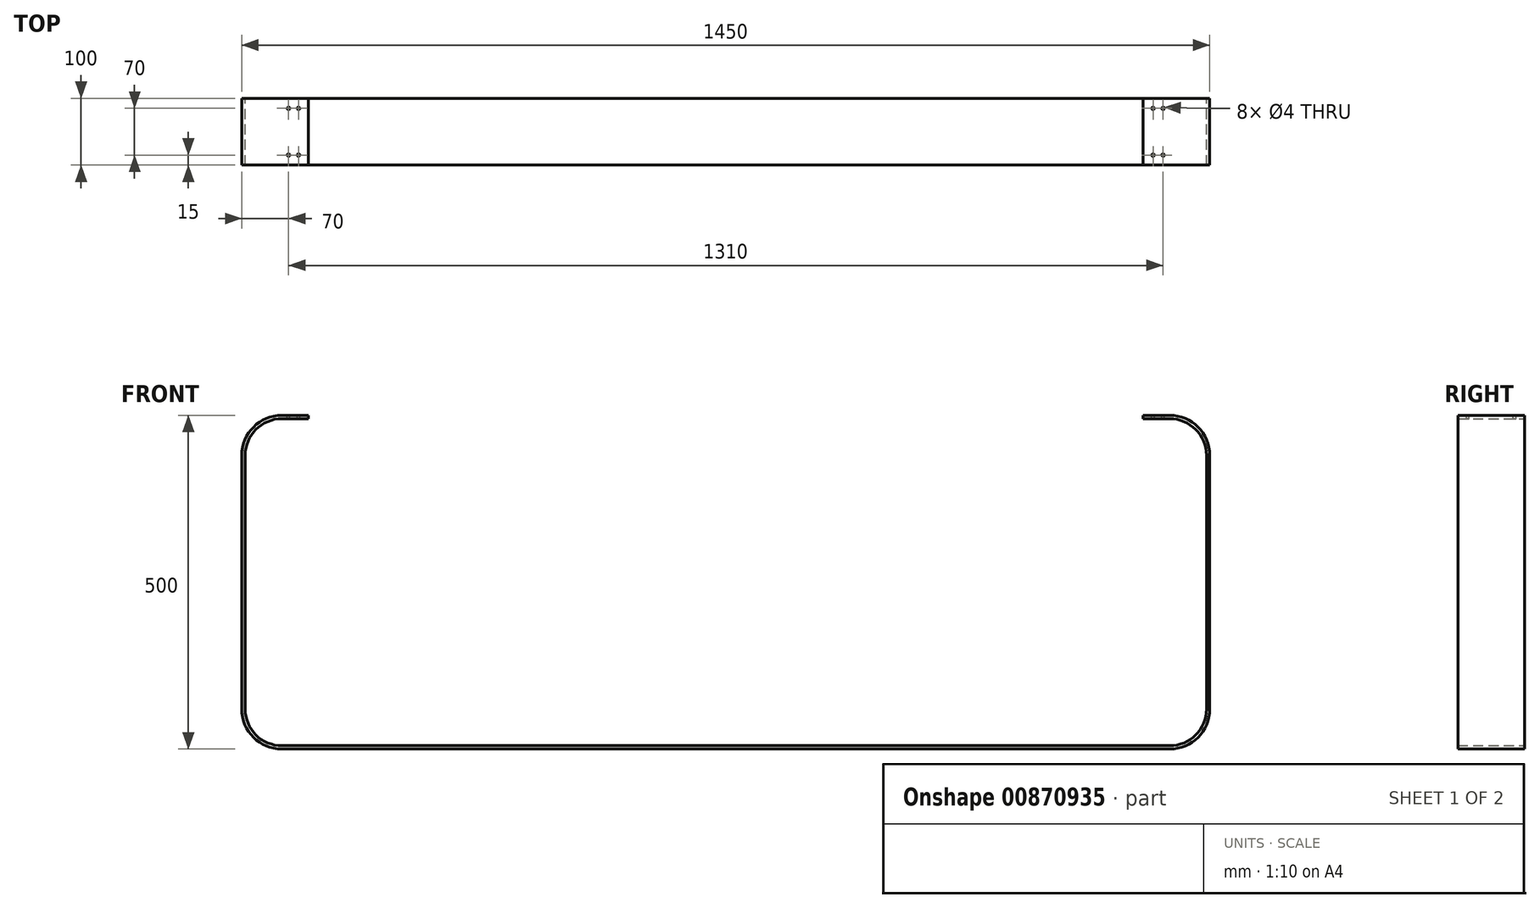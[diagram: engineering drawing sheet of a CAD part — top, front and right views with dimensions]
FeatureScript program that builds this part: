
annotation { "Feature Type Name" : "Feature", "Feature Type Description" : "" }
export const myFeature = defineFeature(function(context is Context, id is Id, definition is map)
    precondition{}
    {
        {
            var Q0;
            Q0=qCreatedBy(makeId("Front.planeOp"),FACE);
            var sketch = newSketch(context, id + "F0", { "sketchPlane" : qUnion([Q0])});
            skLineSegment(sketch, "E0", {"start": v(725, -60) * mm, "end": v(725, -440) * mm});
            skLineSegment(sketch, "E1", {"start": v(665, -500) * mm, "end": v(-665, -500) * mm});
            skLineSegment(sketch, "E2", {"start": v(-725, -440) * mm, "end": v(-725, -60) * mm});
            skPoint(sketch, "E3.visualSharp", {"position": v(725, -500) * mm});
            skArc(sketch, "E3.filletArc", {"start": v(665, -500) * mm, "mid": v(707.43, -482.43) * mm, "end": v(725, -440) * mm});
            skPoint(sketch, "E4.visualSharp", {"position": v(-725, -500) * mm});
            skArc(sketch, "E4.filletArc", {"start": v(-725, -440) * mm, "mid": v(-707.43, -482.43) * mm, "end": v(-665, -500) * mm});
            skLineSegment(sketch, "E5", {"start": v(665, 0) * mm, "end": v(625, 0) * mm});
            skLineSegment(sketch, "E6", {"start": v(-625, 0) * mm, "end": v(-665, 0) * mm});
            skPoint(sketch, "E7.visualSharp", {"position": v(-725, 0) * mm});
            skArc(sketch, "E7.filletArc", {"start": v(-665, 0) * mm, "mid": v(-707.43, -17.57) * mm, "end": v(-725, -60) * mm});
            skPoint(sketch, "E8.visualSharp", {"position": v(725, 0) * mm});
            skArc(sketch, "E8.filletArc", {"start": v(725, -60) * mm, "mid": v(707.43, -17.57) * mm, "end": v(665, 0) * mm});
            skLineSegment(sketch, "E9.0", {"start": v(665, -5) * mm, "end": v(625, -5) * mm});
            skArc(sketch, "E9.1", {"start": v(720, -60) * mm, "mid": v(703.9, -21.1) * mm, "end": v(665, -5) * mm});
            skLineSegment(sketch, "E9.2", {"start": v(720, -60) * mm, "end": v(720, -440) * mm});
            skArc(sketch, "E9.3", {"start": v(665, -495) * mm, "mid": v(703.9, -478.9) * mm, "end": v(720, -440) * mm});
            skLineSegment(sketch, "E9.4", {"start": v(665, -495) * mm, "end": v(-665, -495) * mm});
            skLineSegment(sketch, "E9.5", {"start": v(-625, -5) * mm, "end": v(-665, -5) * mm});
            skArc(sketch, "E9.6", {"start": v(-665, -5) * mm, "mid": v(-703.9, -21.1) * mm, "end": v(-720, -60) * mm});
            skLineSegment(sketch, "E9.7", {"start": v(-720, -440) * mm, "end": v(-720, -60) * mm});
            skArc(sketch, "E9.8", {"start": v(-720, -440) * mm, "mid": v(-703.9, -478.9) * mm, "end": v(-665, -495) * mm});
            skLineSegment(sketch, "E10", {"start": v(625, -5) * mm, "end": v(625, 0) * mm});
            skLineSegment(sketch, "E11", {"start": v(-625, 0) * mm, "end": v(-625, -5) * mm});
            skSolve(sketch);
        }
        {
            var Q0;
            Q0 = qSketchRegion(id + "F0", true);
            extrude(context, id + "F1", {"entities" : qUnion([Q0]), "depth" : 100 * mm, "offsetDistance" : 25 * mm});
        }
        {
            var Q0;
            Q0=makeQuery(id+"F1.opExtrude","SWEPT_FACE",FACE,{"disambiguationData":[OSD([sQuery(id+"F0.wireOp",EDGE,"E6")])]});
            var sketch = newSketch(context, id + "F2", { "sketchPlane" : qUnion([Q0])});
            skCircle(sketch, "E12", {"center": v(-655, -85) * mm, "radius": 2 * mm});
            skCircle(sketch, "E13", {"center": v(-640, -85) * mm, "radius": 2 * mm});
            skCircle(sketch, "E14", {"center": v(-655, -15) * mm, "radius": 2 * mm});
            skCircle(sketch, "E15", {"center": v(-640, -15) * mm, "radius": 2 * mm});
            skCircle(sketch, "E16.MirrorC", {"center": v(640, -15) * mm, "radius": 2 * mm});
            skCircle(sketch, "E17.MirrorC", {"center": v(655, -15) * mm, "radius": 2 * mm});
            skCircle(sketch, "E18.MirrorC", {"center": v(655, -85) * mm, "radius": 2 * mm});
            skCircle(sketch, "E19.MirrorC", {"center": v(640, -85) * mm, "radius": 2 * mm});
            skSolve(sketch);
        }
        {
            var Q0;
            Q0 = qSketchRegion(id + "F2", true);
            extrude(context, id + "F3", {"entities" : qUnion([Q0]), "operationType" : NewBodyOperationType.REMOVE, "endBound" : BoundingType.UP_TO_NEXT, "oppositeDirection" : true, "depth" : 25 * mm, "offsetDistance" : 25 * mm});
        }
    });
